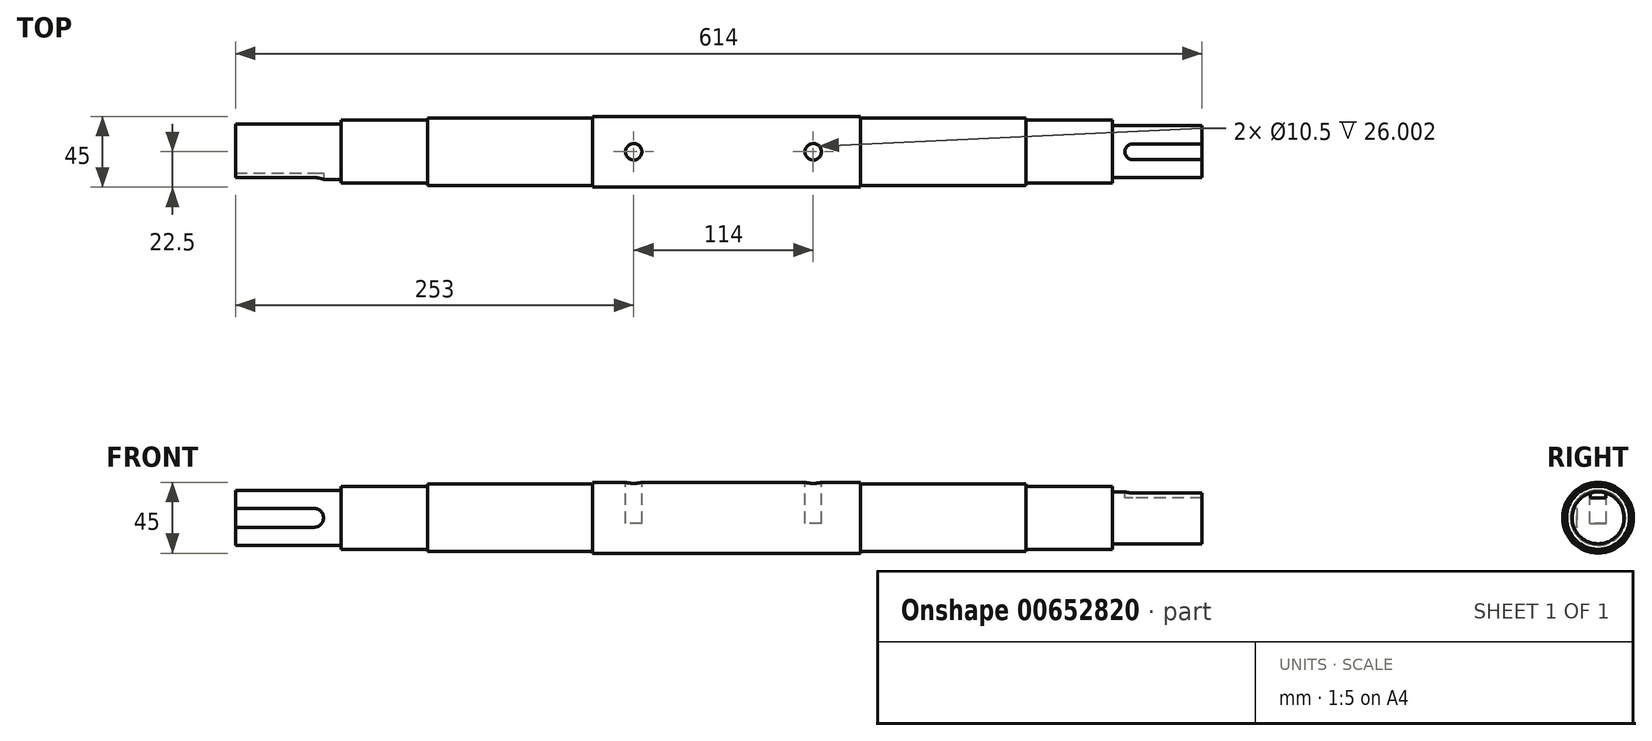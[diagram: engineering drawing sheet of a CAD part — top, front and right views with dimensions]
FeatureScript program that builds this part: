
annotation { "Feature Type Name" : "Feature", "Feature Type Description" : "" }
export const myFeature = defineFeature(function(context is Context, id is Id, definition is map)
    precondition{}
    {
        {
            var Q0;
            Q0=qCreatedBy(makeId("Front.planeOp"),FACE);
            var sketch = newSketch(context, id + "F0", { "sketchPlane" : qUnion([Q0])});
            skLineSegment(sketch, "E0", {"start": v(-307, 0) * mm, "end": v(-307, 17.5) * mm});
            skLineSegment(sketch, "E1", {"start": v(-307, 17.5) * mm, "end": v(-240, 17.5) * mm});
            skLineSegment(sketch, "E2", {"start": v(-240, 17.5) * mm, "end": v(-240, 20) * mm});
            skLineSegment(sketch, "E3", {"start": v(-240, 20) * mm, "end": v(-185, 20) * mm});
            skLineSegment(sketch, "E4", {"start": v(-185, 20) * mm, "end": v(-185, 21.5) * mm});
            skLineSegment(sketch, "E5", {"start": v(-185, 21.5) * mm, "end": v(-80, 21.5) * mm});
            skLineSegment(sketch, "E6", {"start": v(-80, 21.5) * mm, "end": v(-80, 22.5) * mm});
            skLineSegment(sketch, "E7", {"start": v(-80, 22.5) * mm, "end": v(90, 22.5) * mm});
            skLineSegment(sketch, "E8", {"start": v(90, 22.5) * mm, "end": v(90, 21.5) * mm});
            skLineSegment(sketch, "E9", {"start": v(90, 21.5) * mm, "end": v(195, 21.5) * mm});
            skLineSegment(sketch, "E10", {"start": v(195, 21.5) * mm, "end": v(195, 20) * mm});
            skLineSegment(sketch, "E11", {"start": v(195, 20) * mm, "end": v(250, 20) * mm});
            skLineSegment(sketch, "E12", {"start": v(250, 20) * mm, "end": v(250, 16.5) * mm});
            skLineSegment(sketch, "E13", {"start": v(250, 16.5) * mm, "end": v(307, 16.5) * mm});
            skLineSegment(sketch, "E14", {"start": v(307, 16.5) * mm, "end": v(307, 0) * mm});
            skLineSegment(sketch, "E15", {"start": v(307, 0) * mm, "end": v(-307, 0) * mm});
            skSolve(sketch);
        }
        {
            var Q0;
            Q0=makeQuery(id+"F0.imprint","IMPRINT",FACE,{"disambiguationData":[TD([[makeQuery(id+"F0.imprint","IMPRINT",EDGE,{"derivedFrom":sQuery(id+"F0.wireOp",EDGE,"E0")}),-1.0]])]});
            var Q1;
            Q1=sQuery(id+"F0.wireOp",EDGE,"E15");
            revolve(context, id + "F1", {"surfaceOperationType" : NewSurfaceOperationType.NEW, "entities" : qUnion([Q0]), "axis" : qUnion([Q1]), "revolveType" : RevolveType.FULL});
        }
        {
            var Q0;
            Q0=qCreatedBy(makeId("Front.planeOp"),FACE);
            cPlane(context, id + "F2", {"entities" : qUnion([Q0]), "cplaneType" : CPlaneType.OFFSET, "offset" : 17.5 * mm, "width" : 150 * mm, "height" : 150 * mm});
        }
        {
            var Q0;
            Q0=qCreatedBy(id+"F2.planeOp",FACE);
            var sketch = newSketch(context, id + "F3", { "sketchPlane" : qUnion([Q0])});
            skLineSegment(sketch, "E16.bottom", {"start": v(-307, 6) * mm, "end": v(-257, 6) * mm});
            skLineSegment(sketch, "E16.top", {"start": v(-307, -6) * mm, "end": v(-257, -6) * mm});
            skLineSegment(sketch, "E16.left", {"start": v(-307, 6) * mm, "end": v(-307, -6) * mm});
            skLineSegment(sketch, "E17.0", {"start": v(-307, 17.5) * mm, "end": v(-307, -17.5) * mm});
            skArc(sketch, "E18", {"start": v(-257, -6) * mm, "mid": v(-251, 0) * mm, "end": v(-257, 6) * mm});
            skSolve(sketch);
        }
        {
            var Q0;
            {var subQ0=sQuery(id+"F3.wireOp",EDGE,"E16.bottom");Q0=makeQuery(id+"F3.imprint","IMPRINT",FACE,{"disambiguationData":[TD([[makeQuery(id+"F3.imprint","IMPRINT",EDGE,{"derivedFrom":subQ0}),-1.0]])]});}
            extrude(context, id + "F4", {"entities" : qUnion([Q0]), "operationType" : NewBodyOperationType.REMOVE, "oppositeDirection" : true, "depth" : 4 * mm, "offsetDistance" : 25 * mm});
        }
        {
            var Q0;
            Q0=qCreatedBy(makeId("Top.planeOp"),FACE);
            cPlane(context, id + "F5", {"entities" : qUnion([Q0]), "cplaneType" : CPlaneType.OFFSET, "offset" : 16.5 * mm, "width" : 150 * mm, "height" : 150 * mm});
        }
        {
            var Q0;
            Q0=qCreatedBy(id+"F5.planeOp",FACE);
            var sketch = newSketch(context, id + "F6", { "sketchPlane" : qUnion([Q0])});
            skLineSegment(sketch, "E19.0", {"start": v(307, 16.5) * mm, "end": v(307, -16.5) * mm});
            skLineSegment(sketch, "E20.bottom", {"start": v(307, 5) * mm, "end": v(263, 5) * mm});
            skLineSegment(sketch, "E20.top", {"start": v(307, -5) * mm, "end": v(263, -5) * mm});
            skLineSegment(sketch, "E20.left", {"start": v(307, 5) * mm, "end": v(307, -5) * mm});
            skArc(sketch, "E21", {"start": v(263, 5) * mm, "mid": v(258, 0) * mm, "end": v(263, -5) * mm});
            skSolve(sketch);
        }
        {
            var Q0;
            Q0=makeQuery(id+"F6.imprint","IMPRINT",FACE,{"disambiguationData":[TD([[makeQuery(id+"F6.imprint","IMPRINT",EDGE,{"derivedFrom":sQuery(id+"F6.wireOp",EDGE,"E20.bottom")}),1.0]])]});
            extrude(context, id + "F7", {"entities" : qUnion([Q0]), "operationType" : NewBodyOperationType.REMOVE, "oppositeDirection" : true, "depth" : 4 * mm, "offsetDistance" : 25 * mm});
        }
        {
            var Q0;
            Q0=qCreatedBy(makeId("Top.planeOp"),FACE);
            cPlane(context, id + "F8", {"entities" : qUnion([Q0]), "cplaneType" : CPlaneType.OFFSET, "offset" : 22.5 * mm, "width" : 150 * mm, "height" : 150 * mm});
        }
        {
            var Q0;
            Q0=qCreatedBy(id+"F8.planeOp",FACE);
            var sketch = newSketch(context, id + "F9", { "sketchPlane" : qUnion([Q0])});
            skCircle(sketch, "E22", {"center": v(-54, 0) * mm, "radius": 5.25 * mm});
            skCircle(sketch, "E23", {"center": v(60, 0) * mm, "radius": 5.25 * mm});
            skSolve(sketch);
        }
        {
            var Q0;
            Q0=makeQuery(id+"F9.imprint","IMPRINT",FACE,{"disambiguationData":[TD([[makeQuery(id+"F9.imprint","IMPRINT",EDGE,{"derivedFrom":sQuery(id+"F9.wireOp",EDGE,"E22")}),1.0]])]});
            var Q1;
            Q1=makeQuery(id+"F9.imprint","IMPRINT",FACE,{"disambiguationData":[TD([[makeQuery(id+"F9.imprint","IMPRINT",EDGE,{"derivedFrom":sQuery(id+"F9.wireOp",EDGE,"E23")}),1.0]])]});
            extrude(context, id + "F10", {"entities" : qUnion([Q0, Q1]), "operationType" : NewBodyOperationType.REMOVE, "oppositeDirection" : true, "depth" : 26 * mm, "offsetDistance" : 25 * mm});
        }
    });
